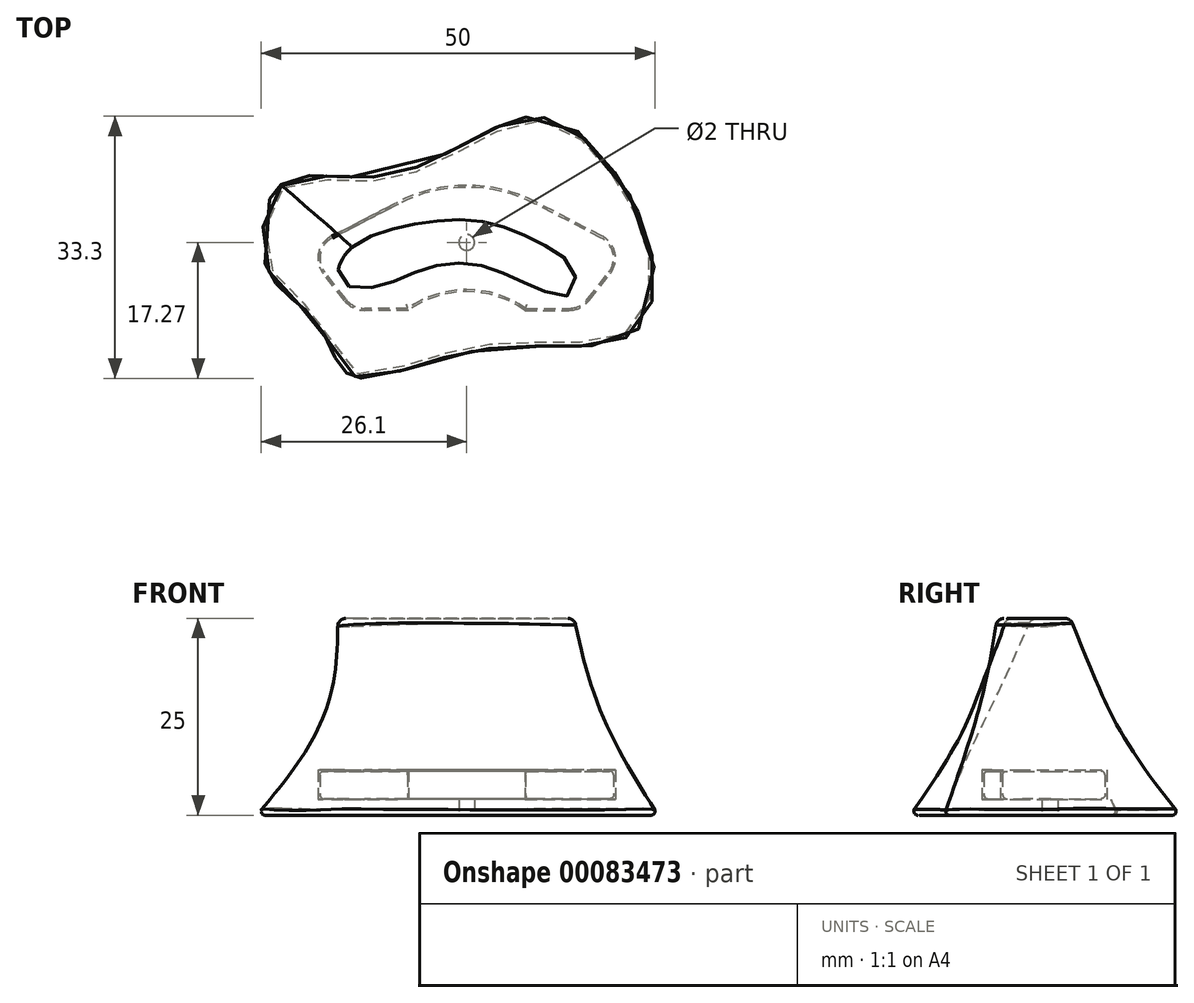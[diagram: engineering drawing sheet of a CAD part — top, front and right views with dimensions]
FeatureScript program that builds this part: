
annotation { "Feature Type Name" : "Feature", "Feature Type Description" : "" }
export const myFeature = defineFeature(function(context is Context, id is Id, definition is map)
    precondition{}
    {
        {
            var Q0;
            Q0=qCreatedBy(makeId("Top.planeOp"),FACE);
            var sketch = newSketch(context, id + "F0", { "sketchPlane" : qUnion([Q0])});
            skArc(sketch, "E0", {"start": v(7.49, -2.37) * mm, "mid": v(0, 0) * mm, "end": v(-7.49, -2.37) * mm});
            skLineSegment(sketch, "E1", {"start": v(7.49, -2.37) * mm, "end": v(12.99, -2.37) * mm});
            skLineSegment(sketch, "E2", {"start": v(-7.49, -2.37) * mm, "end": v(-12.99, -2.37) * mm});
            skLineSegment(sketch, "E3", {"start": v(15.35, -1.22) * mm, "end": v(18.04, 2.21) * mm});
            skLineSegment(sketch, "E4", {"start": v(17.08, 6.58) * mm, "end": v(8.7, 10.9) * mm});
            skLineSegment(sketch, "E5", {"start": v(-15.35, -1.22) * mm, "end": v(-18.04, 2.21) * mm});
            skLineSegment(sketch, "E6", {"start": v(-17.08, 6.58) * mm, "end": v(-8.7, 10.9) * mm});
            skArc(sketch, "E7", {"start": v(8.7, 10.9) * mm, "mid": v(0, 13) * mm, "end": v(-8.7, 10.9) * mm});
            skPoint(sketch, "E8.visualSharp", {"position": v(20.2, 4.98) * mm});
            skArc(sketch, "E8.filletArc", {"start": v(18.04, 2.21) * mm, "mid": v(18.58, 4.62) * mm, "end": v(17.08, 6.58) * mm});
            skPoint(sketch, "E9.visualSharp", {"position": v(-20.2, 4.98) * mm});
            skArc(sketch, "E9.filletArc", {"start": v(-17.08, 6.58) * mm, "mid": v(-18.58, 4.62) * mm, "end": v(-18.04, 2.21) * mm});
            skPoint(sketch, "E10.visualSharp", {"position": v(14.45, -2.37) * mm});
            skArc(sketch, "E10.filletArc", {"start": v(12.99, -2.37) * mm, "mid": v(14.3, -2.07) * mm, "end": v(15.35, -1.22) * mm});
            skPoint(sketch, "E11.visualSharp", {"position": v(-14.45, -2.37) * mm});
            skArc(sketch, "E11.filletArc", {"start": v(-15.35, -1.22) * mm, "mid": v(-14.3, -2.07) * mm, "end": v(-12.99, -2.37) * mm});
            skLineSegment(sketch, "E12", {"start": v(0, 0) * mm, "end": v(0, 13) * mm, "construction": true});
            skLineSegment(sketch, "E13", {"start": v(15.75, 4) * mm, "end": v(-15.75, 4) * mm, "construction": true});
            skPoint(sketch, "E14", {"position": v(0, 4) * mm});
            skSolve(sketch);
        }
        {
            var Q0;
            Q0=qCreatedBy(makeId("Top.planeOp"),FACE);
            cPlane(context, id + "F1", {"entities" : qUnion([Q0]), "cplaneType" : CPlaneType.OFFSET, "offset" : 2 * mm, "width" : 150 * mm, "height" : 150 * mm});
        }
        {
            var Q0;
            Q0=qCreatedBy(id+"F1.planeOp",FACE);
            var sketch = newSketch(context, id + "F2", { "sketchPlane" : qUnion([Q0])});
            skArc(sketch, "E15.0", {"start": v(8.7, 10.9) * mm, "mid": v(0, 13) * mm, "end": v(-8.7, 10.9) * mm});
            skLineSegment(sketch, "E16.0", {"start": v(17.08, 6.58) * mm, "end": v(8.7, 10.9) * mm});
            skArc(sketch, "E17.0", {"start": v(18.04, 2.21) * mm, "mid": v(18.58, 4.62) * mm, "end": v(17.08, 6.58) * mm});
            skLineSegment(sketch, "E18.0", {"start": v(15.35, -1.22) * mm, "end": v(18.04, 2.21) * mm});
            skArc(sketch, "E19.0", {"start": v(12.99, -2.37) * mm, "mid": v(14.3, -2.07) * mm, "end": v(15.35, -1.22) * mm});
            skLineSegment(sketch, "E20.0", {"start": v(7.49, -2.37) * mm, "end": v(12.99, -2.37) * mm});
            skArc(sketch, "E21.0", {"start": v(7.49, -2.37) * mm, "mid": v(0, 0) * mm, "end": v(-7.49, -2.37) * mm});
            skLineSegment(sketch, "E22.0", {"start": v(-7.49, -2.37) * mm, "end": v(-12.99, -2.37) * mm});
            skArc(sketch, "E23.0", {"start": v(-15.35, -1.22) * mm, "mid": v(-14.3, -2.07) * mm, "end": v(-12.99, -2.37) * mm});
            skLineSegment(sketch, "E24.0", {"start": v(-15.35, -1.22) * mm, "end": v(-18.04, 2.21) * mm});
            skArc(sketch, "E25.0", {"start": v(-17.08, 6.58) * mm, "mid": v(-18.58, 4.62) * mm, "end": v(-18.04, 2.21) * mm});
            skLineSegment(sketch, "E26.0", {"start": v(-17.08, 6.58) * mm, "end": v(-8.7, 10.9) * mm});
            skLineSegment(sketch, "E27.0", {"start": v(17.2, 6.8) * mm, "end": v(8.81, 11.12) * mm});
            skArc(sketch, "E27.1", {"start": v(-15.55, -1.37) * mm, "mid": v(-14.41, -2.3) * mm, "end": v(-12.99, -2.62) * mm});
            skLineSegment(sketch, "E27.2", {"start": v(-15.55, -1.37) * mm, "end": v(-18.23, 2.06) * mm});
            skArc(sketch, "E27.3", {"start": v(-17.2, 6.8) * mm, "mid": v(-18.83, 4.68) * mm, "end": v(-18.23, 2.06) * mm});
            skLineSegment(sketch, "E27.4", {"start": v(-17.2, 6.8) * mm, "end": v(-8.81, 11.12) * mm});
            skLineSegment(sketch, "E27.5", {"start": v(-7.4, -2.62) * mm, "end": v(-12.99, -2.62) * mm});
            skArc(sketch, "E27.6", {"start": v(8.81, 11.12) * mm, "mid": v(0, 13.25) * mm, "end": v(-8.81, 11.12) * mm});
            skArc(sketch, "E27.7", {"start": v(7.4, -2.62) * mm, "mid": v(0, -0.25) * mm, "end": v(-7.4, -2.62) * mm});
            skLineSegment(sketch, "E27.8", {"start": v(7.4, -2.62) * mm, "end": v(12.99, -2.62) * mm});
            skArc(sketch, "E27.9", {"start": v(12.99, -2.62) * mm, "mid": v(14.41, -2.3) * mm, "end": v(15.55, -1.37) * mm});
            skLineSegment(sketch, "E27.10", {"start": v(15.55, -1.37) * mm, "end": v(18.23, 2.06) * mm});
            skArc(sketch, "E27.11", {"start": v(18.23, 2.06) * mm, "mid": v(18.83, 4.68) * mm, "end": v(17.2, 6.8) * mm});
            skSolve(sketch);
        }
        {
            var Q0;
            Q0=makeQuery(id+"F2.imprint","IMPRINT",FACE,{"disambiguationData":[TD([[makeQuery(id+"F2.imprint","IMPRINT",EDGE,{"derivedFrom":sQuery(id+"F2.wireOp",EDGE,"E15.0")}),1.0]])]});
            var Q1;
            Q1=makeQuery(id+"F2.imprint","IMPRINT",FACE,{"disambiguationData":[TD([[makeQuery(id+"F2.imprint","IMPRINT",EDGE,{"derivedFrom":sQuery(id+"F2.wireOp",EDGE,"E15.0")}),-1.0]])]});
            extrude(context, id + "F3", {"entities" : qUnion([Q0, Q1]), "depth" : 3.75 * mm});
        }
        {
            var Q0;
            Q0=makeQuery(id+"F0.imprint","IMPRINT",FACE,{"disambiguationData":[TD([[makeQuery(id+"F0.imprint","IMPRINT",EDGE,{"derivedFrom":sQuery(id+"F0.wireOp",EDGE,"E0")}),-1.0]])]});
            extrude(context, id + "F4", {"entities" : qUnion([Q0]), "depth" : 3.5 * mm});
        }
        {
            var Q0;
            Q0=makeQuery(id+"F4.opExtrude","CAP_EDGE",EDGE,{"disambiguationData":[OSD([sQuery(id+"F0.wireOp",EDGE,"E5")])],"isStart":false});
            var Q1;
            Q1=makeQuery(id+"F4.opExtrude","CAP_EDGE",EDGE,{"disambiguationData":[OSD([sQuery(id+"F0.wireOp",EDGE,"E0")])],"isStart":false});
            var Q2;
            Q2=makeQuery(id+"F4.opExtrude","CAP_EDGE",EDGE,{"disambiguationData":[OSD([sQuery(id+"F0.wireOp",EDGE,"E0")])],"isStart":true});
            var Q3;
            Q3=makeQuery(id+"F4.opExtrude","CAP_EDGE",EDGE,{"disambiguationData":[OSD([sQuery(id+"F0.wireOp",EDGE,"E2")])],"isStart":true});
            fillet(context, id + "F5", {"entities" : qUnion([Q0, Q1, Q2, Q3]), "radius" : .5 * mm, "tangentPropagation" : true, "allowEdgeOverflow" : false});
        }
        {
            var Q0;
            Q0=makeQuery(id+"F4.opExtrude","SWEPT_BODY",BODY,{"disambiguationData":[OSD([sQuery(id+"F0.wireOp",EDGE,"E0"),sQuery(id+"F0.wireOp",EDGE,"E1"),sQuery(id+"F0.wireOp",EDGE,"E2"),sQuery(id+"F0.wireOp",EDGE,"E3"),sQuery(id+"F0.wireOp",EDGE,"E4"),sQuery(id+"F0.wireOp",EDGE,"E5"),sQuery(id+"F0.wireOp",EDGE,"E6"),sQuery(id+"F0.wireOp",EDGE,"E7"),sQuery(id+"F0.wireOp",EDGE,"E8.filletArc"),sQuery(id+"F0.wireOp",EDGE,"E9.filletArc"),sQuery(id+"F0.wireOp",EDGE,"E10.filletArc"),sQuery(id+"F0.wireOp",EDGE,"E11.filletArc")])]});
            transform(context, id + "F6", {"entities" : qUnion([Q0]), "transformType" : TransformType.TRANSLATION_3D, "dx" : 0 * mm, "dy" : 0 * mm, "dz" : 2.1 * mm, "makeCopy" : false});
        }
        {
            var Q0;
            Q0=qCreatedBy(makeId("Top.planeOp"),FACE);
            var sketch = newSketch(context, id + "F7", { "sketchPlane" : qUnion([Q0])});
            skFitSpline(sketch, "E28", {"points": [v(-24.1, 13.85) * mm, v(-9.52, 14.77) * mm, v(8.47, 22.52) * mm, v(17.53, 17.53) * mm, v(23.96, 4.66) * mm, v(21.47, -5.84) * mm, v(1.64, -7.94) * mm, v(-15.17, -11.36) * mm, v(-19.24, -4.27) * mm, v(-25.8, 2.7) * mm, v(-24.1, 13.85) * mm]});
            skSolve(sketch);
        }
        {
            var Q0;
            Q0=qCreatedBy(makeId("Top.planeOp"),FACE);
            cPlane(context, id + "F8", {"entities" : qUnion([Q0]), "cplaneType" : CPlaneType.OFFSET, "offset" : 25 * mm, "width" : 150 * mm, "height" : 150 * mm});
        }
        {
            var Q0;
            Q0=qCreatedBy(id+"F8.planeOp",FACE);
            var sketch = newSketch(context, id + "F9", { "sketchPlane" : qUnion([Q0])});
            skFitSpline(sketch, "E29", {"points": [v(-15.13, 4.84) * mm, v(-8.23, 7.78) * mm, v(1.99, 8.43) * mm, v(8.85, 5.94) * mm, v(13.23, 2.78) * mm, v(12.93, -0.6) * mm, v(1.12, 3.48) * mm, v(-8.94, 1.48) * mm, v(-12.84, 0.45) * mm, v(-16.13, 1.24) * mm, v(-15.13, 4.84) * mm]});
            skSolve(sketch);
        }
        {
            var Q0;
            Q0=qCreatedBy(makeId("Top.planeOp"),FACE);
            cPlane(context, id + "F10", {"entities" : qUnion([Q0]), "cplaneType" : CPlaneType.OFFSET, "offset" : 15 * mm, "width" : 150 * mm, "height" : 150 * mm});
        }
        {
            var Q0;
            Q0=qCreatedBy(id+"F10.planeOp",FACE);
            var sketch = newSketch(context, id + "F11", { "sketchPlane" : qUnion([Q0])});
            skFitSpline(sketch, "E30", {"points": [v(-15.56, 5.78) * mm, v(-11.69, 9.05) * mm, v(-4, 12.37) * mm, v(5.81, 11.85) * mm, v(12.19, 7.95) * mm, v(16.1, 2.57) * mm, v(15.23, -1.5) * mm, v(7.7, -2.33) * mm, v(-0.04, -0.85) * mm, v(-7.15, -2.6) * mm, v(-12.63, -3.05) * mm, v(-16.59, -0.68) * mm, v(-17.32, 2.15) * mm, v(-15.56, 5.78) * mm]});
            skSolve(sketch);
        }
        {
            var Q1;
            Q1=makeQuery(id+"F7.imprint","IMPRINT",FACE,{"disambiguationData":[TD([[makeQuery(id+"F7.imprint","IMPRINT",EDGE,{"derivedFrom":sQuery(id+"F7.wireOp",EDGE,"E28")}),-1.0]])]});
            var Q2;
            Q2=makeQuery(id+"F11.imprint","IMPRINT",FACE,{"disambiguationData":[TD([[makeQuery(id+"F11.imprint","IMPRINT",EDGE,{"derivedFrom":sQuery(id+"F11.wireOp",EDGE,"E30")}),-1.0]])]});
            var Q3;
            Q3=makeQuery(id+"F9.imprint","IMPRINT",FACE,{"disambiguationData":[TD([[makeQuery(id+"F9.imprint","IMPRINT",EDGE,{"derivedFrom":sQuery(id+"F9.wireOp",EDGE,"E29")}),-1.0]])]});
            loft(context, id + "F12", {"sheetProfilesArray" : [{ "sheetProfileEntities" : qUnion([Q1]) }, { "sheetProfileEntities" : qUnion([Q2]) }, { "sheetProfileEntities" : qUnion([Q3]) }]});
        }
        {
            var Q0;
            Q0=makeQuery(id+"F12.opLoft","CAP_FACE",FACE,{"disambiguationData":[OSD([makeQuery(id+"F7.imprint","IMPRINT",FACE,{"disambiguationData":[TD([[makeQuery(id+"F7.imprint","IMPRINT",EDGE,{"derivedFrom":sQuery(id+"F7.wireOp",EDGE,"E28")}),-1.0]])]})])],"isStart":true});
            var sketch = newSketch(context, id + "F13", { "sketchPlane" : qUnion([Q0])});
            skCircle(sketch, "E31", {"center": v(0, -6) * mm, "radius": 1 * mm});
            skLineSegment(sketch, "E32", {"start": v(0, 0) * mm, "end": v(0, -6) * mm, "construction": true});
            skSolve(sketch);
        }
        {
            var Q0;
            Q0=makeQuery(id+"F13.imprint","IMPRINT",FACE,{"disambiguationData":[TD([[makeQuery(id+"F13.imprint","IMPRINT",EDGE,{"derivedFrom":sQuery(id+"F13.wireOp",EDGE,"E31")}),1.0]])]});
            var Q1;
            Q1=makeQuery(id+"F3.opExtrude","CAP_FACE",FACE,{"disambiguationData":[OSD([sQuery(id+"F2.wireOp",EDGE,"E27.0"),sQuery(id+"F2.wireOp",EDGE,"E27.1"),sQuery(id+"F2.wireOp",EDGE,"E27.2"),sQuery(id+"F2.wireOp",EDGE,"E27.3"),sQuery(id+"F2.wireOp",EDGE,"E27.4"),sQuery(id+"F2.wireOp",EDGE,"E27.5"),sQuery(id+"F2.wireOp",EDGE,"E27.6"),sQuery(id+"F2.wireOp",EDGE,"E27.7"),sQuery(id+"F2.wireOp",EDGE,"E27.8"),sQuery(id+"F2.wireOp",EDGE,"E27.9"),sQuery(id+"F2.wireOp",EDGE,"E27.10"),sQuery(id+"F2.wireOp",EDGE,"E27.11")])],"isStart":true});
            extrude(context, id + "F14", {"entities" : qUnion([Q0]), "operationType" : NewBodyOperationType.REMOVE, "endBound" : BoundingType.UP_TO_SURFACE, "oppositeDirection" : true, "endBoundEntityFace" : qUnion([Q1]), "depth" : 25 * mm});
        }
        {
            var Q0;
            Q0=makeQuery(id+"F3.opExtrude","SWEPT_BODY",BODY,{"disambiguationData":[OSD([sQuery(id+"F2.wireOp",EDGE,"E27.0"),sQuery(id+"F2.wireOp",EDGE,"E27.1"),sQuery(id+"F2.wireOp",EDGE,"E27.2"),sQuery(id+"F2.wireOp",EDGE,"E27.3"),sQuery(id+"F2.wireOp",EDGE,"E27.4"),sQuery(id+"F2.wireOp",EDGE,"E27.5"),sQuery(id+"F2.wireOp",EDGE,"E27.6"),sQuery(id+"F2.wireOp",EDGE,"E27.7"),sQuery(id+"F2.wireOp",EDGE,"E27.8"),sQuery(id+"F2.wireOp",EDGE,"E27.9"),sQuery(id+"F2.wireOp",EDGE,"E27.10"),sQuery(id+"F2.wireOp",EDGE,"E27.11")])]});
            var Q1;
            Q1=makeQuery(id+"F12.opLoft","SWEPT_BODY",BODY,{"disambiguationData":[OSD([makeQuery(id+"F7.imprint","IMPRINT",FACE,{"disambiguationData":[TD([[makeQuery(id+"F7.imprint","IMPRINT",EDGE,{"derivedFrom":sQuery(id+"F7.wireOp",EDGE,"E28")}),-1.0]])]}),makeQuery(id+"F9.imprint","IMPRINT",FACE,{"disambiguationData":[TD([[makeQuery(id+"F9.imprint","IMPRINT",EDGE,{"derivedFrom":sQuery(id+"F9.wireOp",EDGE,"E29")}),-1.0]])]})])]});
            booleanBodies(context, id + "F15", {"operationType" : BooleanOperationType.SUBTRACTION, "tools" : qUnion([Q0]), "targets" : qUnion([Q1])});
        }
        {
            var Q0;
            Q0=makeQuery(id+"F12.opLoft","MID_CAP_EDGE",EDGE,{"disambiguationData":[OSD([sQuery(id+"F7.wireOp",EDGE,"E28")])],"capPos":0.0});
            fillet(context, id + "F16", {"entities" : qUnion([Q0]), "radius" : 0.5 * mm, "tangentPropagation" : true, "allowEdgeOverflow" : false});
        }
        {
            var Q0;
            Q0=makeQuery(id+"F12.opLoft","MID_CAP_EDGE",EDGE,{"disambiguationData":[OSD([sQuery(id+"F7.wireOp",EDGE,"E28"),sQuery(id+"F9.wireOp",EDGE,"E29")])],"capPos":2.0});
            fillet(context, id + "F17", {"entities" : qUnion([Q0]), "radius" : 1 * mm, "tangentPropagation" : true, "allowEdgeOverflow" : false});
        }
    });
